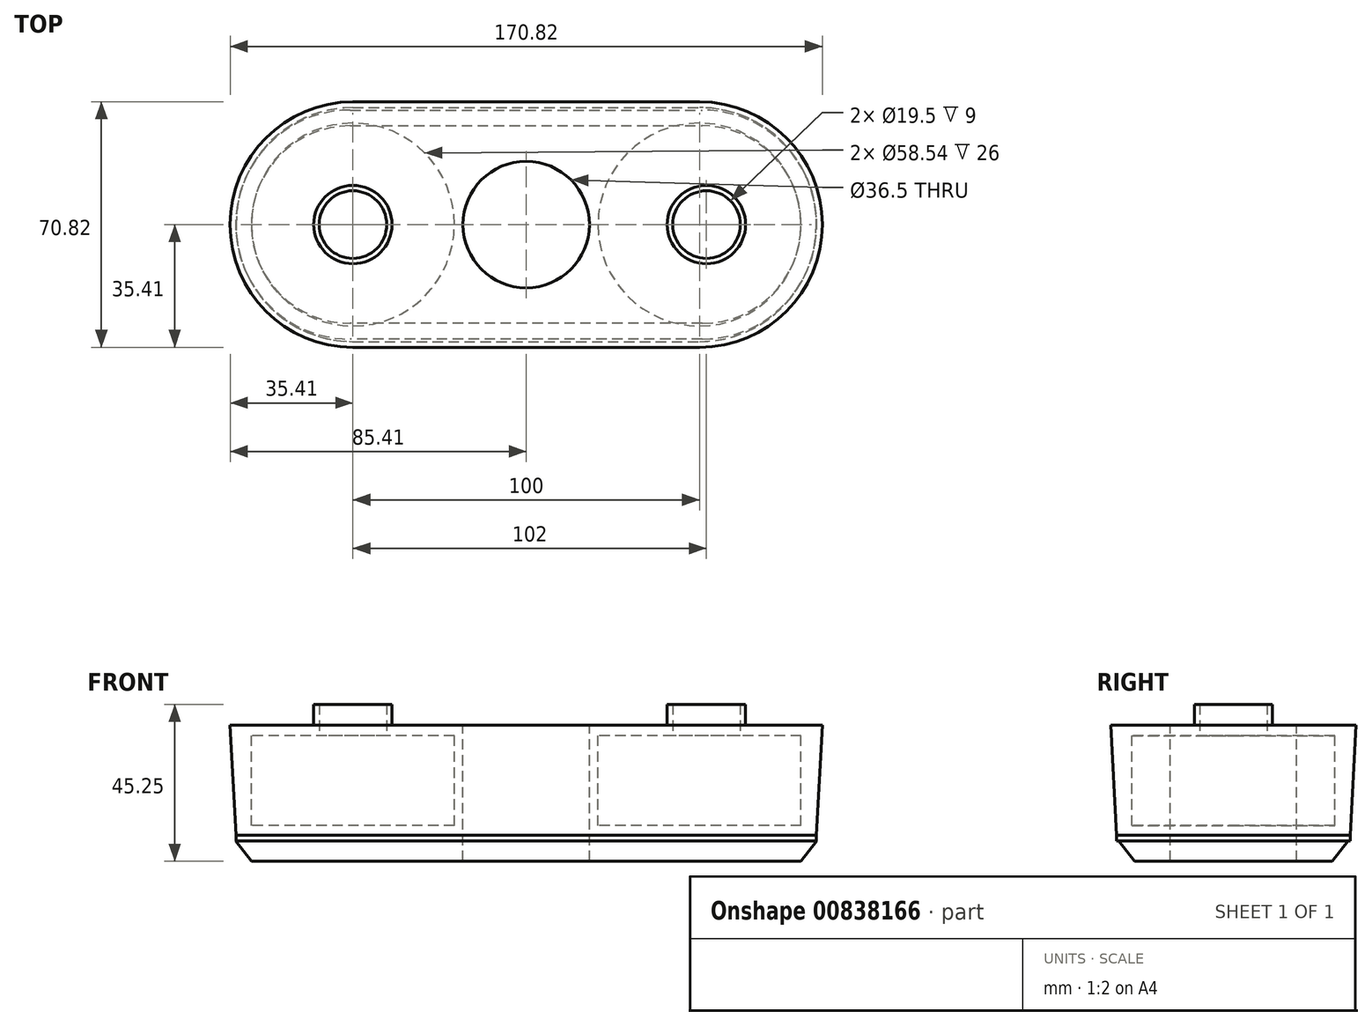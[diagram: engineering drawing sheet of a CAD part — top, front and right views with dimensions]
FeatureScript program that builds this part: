
annotation { "Feature Type Name" : "Feature", "Feature Type Description" : "" }
export const myFeature = defineFeature(function(context is Context, id is Id, definition is map)
    precondition{}
    {
        {
            var Q0;
            Q0=qCreatedBy(makeId("Top.planeOp"),FACE);
            var sketch = newSketch(context, id + "F0", { "sketchPlane" : qUnion([Q0])});
            skCircle(sketch, "E0", {"center": v(0, 0) * mm, "radius": 18.5 * mm, "construction": true});
            skLineSegment(sketch, "E1", {"start": v(-187.5, 0) * mm, "end": v(196.03, 0) * mm, "construction": true});
            skLineSegment(sketch, "E2", {"start": v(0, 122.24) * mm, "end": v(0, -114.7) * mm, "construction": true});
            skPoint(sketch, "E3", {"position": v(-50.8, 0) * mm});
            skArc(sketch, "E4", {"start": v(-50.8, 28.5) * mm, "mid": v(-79.3, 0) * mm, "end": v(-50.8, -28.5) * mm});
            skArc(sketch, "E5.MirrorC", {"start": v(50.8, 28.5) * mm, "mid": v(79.3, 0) * mm, "end": v(50.8, -28.5) * mm});
            skLineSegment(sketch, "E6", {"start": v(-50.8, 28.5) * mm, "end": v(50.8, 28.5) * mm});
            skLineSegment(sketch, "E7", {"start": v(-50.8, -28.5) * mm, "end": v(50.8, -28.5) * mm});
            skSolve(sketch);
        }
        {
            var Q0;
            Q0=qCreatedBy(makeId("Top.planeOp"),FACE);
            cPlane(context, id + "F1", {"entities" : qUnion([Q0]), "cplaneType" : CPlaneType.OFFSET, "offset" : 5.8 * mm, "width" : 150 * mm, "height" : 150 * mm});
        }
        {
            var Q0;
            Q0=qCreatedBy(id+"F1.planeOp",FACE);
            var sketch = newSketch(context, id + "F2", { "sketchPlane" : qUnion([Q0])});
            skArc(sketch, "E8", {"start": v(50, -32.5) * mm, "mid": v(82.5, 0) * mm, "end": v(50, 32.5) * mm});
            skArc(sketch, "E9.MirrorC", {"start": v(-50, -32.5) * mm, "mid": v(-82.5, 0) * mm, "end": v(-50, 32.5) * mm});
            skLineSegment(sketch, "E10", {"start": v(50, -32.5) * mm, "end": v(-50, -32.5) * mm});
            skLineSegment(sketch, "E11", {"start": v(50, 32.5) * mm, "end": v(-50, 32.5) * mm});
            skSolve(sketch);
        }
        {
            var Q0;
            Q0=makeQuery(id+"F0.imprint","IMPRINT",FACE,{"disambiguationData":[TD([[makeQuery(id+"F0.imprint","IMPRINT",EDGE,{"derivedFrom":sQuery(id+"F0.wireOp",EDGE,"E4")}),1.0]])]});
            extrude(context, id + "F3", {"entities" : qUnion([Q0]), "depth" : 5.8 * mm, "offsetDistance" : 25 * mm, "hasDraft" : true, "draftAngle" : 38 * degree});
        }
        {
            var Q0;
            Q0=makeQuery(id+"F2.imprint","IMPRINT",FACE,{"disambiguationData":[TD([[makeQuery(id+"F2.imprint","IMPRINT",EDGE,{"derivedFrom":sQuery(id+"F2.wireOp",EDGE,"E8")}),1.0]])]});
            var sketch = newSketch(context, id + "F4", { "sketchPlane" : qUnion([Q0])});
            skPoint(sketch, "E12.0", {"position": v(-50, 0) * mm});
            skArc(sketch, "E13", {"start": v(-50, 33.75) * mm, "mid": v(-83.75, 0) * mm, "end": v(-50, -33.75) * mm});
            skArc(sketch, "E14.MirrorC", {"start": v(50, 33.75) * mm, "mid": v(83.75, 0) * mm, "end": v(50, -33.75) * mm});
            skLineSegment(sketch, "E15", {"start": v(-50, -33.75) * mm, "end": v(50, -33.75) * mm});
            skLineSegment(sketch, "E16", {"start": v(-50, 33.75) * mm, "end": v(50, 33.75) * mm});
            skSolve(sketch);
        }
        {
            var Q0;
            Q0 = qSketchRegion(id + "F4", true);
            extrude(context, id + "F5", {"entities" : qUnion([Q0]), "operationType" : NewBodyOperationType.ADD, "depth" : 1.7 * mm, "offsetDistance" : 25 * mm});
        }
        {
            var Q0;
            Q0=makeQuery(id+"F5.opExtrude","CAP_FACE",FACE,{"disambiguationData":[OSD([sQuery(id+"F4.wireOp",EDGE,"E13"),sQuery(id+"F4.wireOp",EDGE,"E14.MirrorC"),sQuery(id+"F4.wireOp",EDGE,"E15"),sQuery(id+"F4.wireOp",EDGE,"E16")])],"isStart":false});
            extrude(context, id + "F6", {"entities" : qUnion([Q0]), "operationType" : NewBodyOperationType.ADD, "depth" : 31.75 * mm, "offsetDistance" : 25 * mm, "hasDraft" : true, "draftAngle" : 3 * degree});
        }
        {
            var Q0;
            Q0=makeQuery(id+"F6.opExtrude","CAP_FACE",FACE,{"disambiguationData":[OSD([sQuery(id+"F4.wireOp",EDGE,"E13"),sQuery(id+"F4.wireOp",EDGE,"E14.MirrorC"),sQuery(id+"F4.wireOp",EDGE,"E15"),sQuery(id+"F4.wireOp",EDGE,"E16")])],"isStart":false});
            var sketch = newSketch(context, id + "F7", { "sketchPlane" : qUnion([Q0])});
            skCircle(sketch, "E17", {"center": v(0, 0) * mm, "radius": 18.25 * mm});
            skCircle(sketch, "E18", {"center": v(-50, 0) * mm, "radius": 11.3 * mm});
            skCircle(sketch, "E19", {"center": v(50, 0) * mm, "radius": 11.3 * mm});
            skCircle(sketch, "E20", {"center": v(50, 0) * mm, "radius": 9.75 * mm});
            skCircle(sketch, "E21", {"center": v(-50, 0) * mm, "radius": 9.75 * mm});
            skSolve(sketch);
        }
        {
            var Q0;
            Q0=makeQuery(id+"F7.imprint","IMPRINT",FACE,{"disambiguationData":[TD([[makeQuery(id+"F7.imprint","IMPRINT",EDGE,{"derivedFrom":sQuery(id+"F7.wireOp",EDGE,"E17")}),1.0]])]});
            extrude(context, id + "F8", {"entities" : qUnion([Q0]), "operationType" : NewBodyOperationType.REMOVE, "endBound" : BoundingType.THROUGH_ALL, "oppositeDirection" : true, "depth" : 25 * mm, "offsetDistance" : 25 * mm});
        }
        {
            var Q0;
            Q0=makeQuery(id+"F6.opExtrude","CAP_FACE",FACE,{"disambiguationData":[OSD([sQuery(id+"F4.wireOp",EDGE,"E13"),sQuery(id+"F4.wireOp",EDGE,"E14.MirrorC"),sQuery(id+"F4.wireOp",EDGE,"E15"),sQuery(id+"F4.wireOp",EDGE,"E16")])],"isStart":false});
            var sketch = newSketch(context, id + "F9", { "sketchPlane" : qUnion([Q0])});
            skCircle(sketch, "E22", {"center": v(-50, 0) * mm, "radius": 11.3 * mm});
            skCircle(sketch, "E23", {"center": v(52, 0) * mm, "radius": 11.3 * mm});
            skCircle(sketch, "E24", {"center": v(52, 0) * mm, "radius": 9.75 * mm});
            skCircle(sketch, "E25", {"center": v(-50, 0) * mm, "radius": 9.75 * mm});
            skSolve(sketch);
        }
        {
            var Q0;
            Q0 = qSketchRegion(id + "F9", true);
            extrude(context, id + "F10", {"entities" : qUnion([Q0]), "operationType" : NewBodyOperationType.ADD, "depth" : 6 * mm, "offsetDistance" : 25 * mm});
        }
        {
            var Q0;
            {var subQ0=sQuery(id+"F4.wireOp",EDGE,"E16");var subQ1=sQuery(id+"F4.wireOp",EDGE,"E15");var subQ2=sQuery(id+"F4.wireOp",EDGE,"E14.MirrorC");var subQ3=sQuery(id+"F4.wireOp",EDGE,"E13");Q0=makeQuery(id+"F10.boolean.opBoolean","SPLIT",FACE,{"disambiguationData":[TD([makeQuery(id+"F6.opExtrude","SWEPT_FACE",FACE,{"disambiguationData":[OSD([subQ3])]})])],"derivedFrom":makeQuery(id+"F6.opExtrude","CAP_FACE",FACE,{"disambiguationData":[OSD([subQ3,subQ2,subQ1,subQ0])],"isStart":false})});}
            cPlane(context, id + "F11", {"entities" : qUnion([Q0]), "cplaneType" : CPlaneType.OFFSET, "offset" : 3 * mm, "oppositeDirection" : true, "width" : 150 * mm, "height" : 150 * mm});
        }
        {
            var Q0;
            Q0=qCreatedBy(id+"F11.planeOp",FACE);
            var sketch = newSketch(context, id + "F12", { "sketchPlane" : qUnion([Q0])});
            skPoint(sketch, "E26.0", {"position": v(-50, 0) * mm});
            skCircle(sketch, "E27", {"center": v(-50, 0) * mm, "radius": 29.27 * mm});
            skCircle(sketch, "E28.MirrorC", {"center": v(50, 0) * mm, "radius": 29.27 * mm});
            skSolve(sketch);
        }
        {
            var Q0;
            Q0 = qSketchRegion(id + "F12", true);
            extrude(context, id + "F13", {"entities" : qUnion([Q0]), "operationType" : NewBodyOperationType.REMOVE, "oppositeDirection" : true, "depth" : 26 * mm, "offsetDistance" : 25 * mm});
        }
        {
            var Q0;
            Q0=makeQuery(id+"F10.boolean.opBoolean","SPLIT",FACE,{"disambiguationData":[TD([makeQuery(id+"F10.opExtrude","SWEPT_FACE",FACE,{"disambiguationData":[OSD([sQuery(id+"F9.wireOp",EDGE,"E25")])]})])],"derivedFrom":makeQuery(id+"F6.opExtrude","CAP_FACE",FACE,{"disambiguationData":[OSD([sQuery(id+"F4.wireOp",EDGE,"E13"),sQuery(id+"F4.wireOp",EDGE,"E14.MirrorC"),sQuery(id+"F4.wireOp",EDGE,"E15"),sQuery(id+"F4.wireOp",EDGE,"E16")])],"isStart":false})});
            var Q1;
            Q1=makeQuery(id+"F10.boolean.opBoolean","SPLIT",FACE,{"disambiguationData":[TD([makeQuery(id+"F10.opExtrude","SWEPT_FACE",FACE,{"disambiguationData":[OSD([sQuery(id+"F9.wireOp",EDGE,"E24")])]})])],"derivedFrom":makeQuery(id+"F6.opExtrude","CAP_FACE",FACE,{"disambiguationData":[OSD([sQuery(id+"F4.wireOp",EDGE,"E13"),sQuery(id+"F4.wireOp",EDGE,"E14.MirrorC"),sQuery(id+"F4.wireOp",EDGE,"E15"),sQuery(id+"F4.wireOp",EDGE,"E16")])],"isStart":false})});
            extrude(context, id + "F14", {"entities" : qUnion([Q0, Q1]), "operationType" : NewBodyOperationType.REMOVE, "oppositeDirection" : true, "depth" : 5 * mm, "offsetDistance" : 25 * mm});
        }
    });
